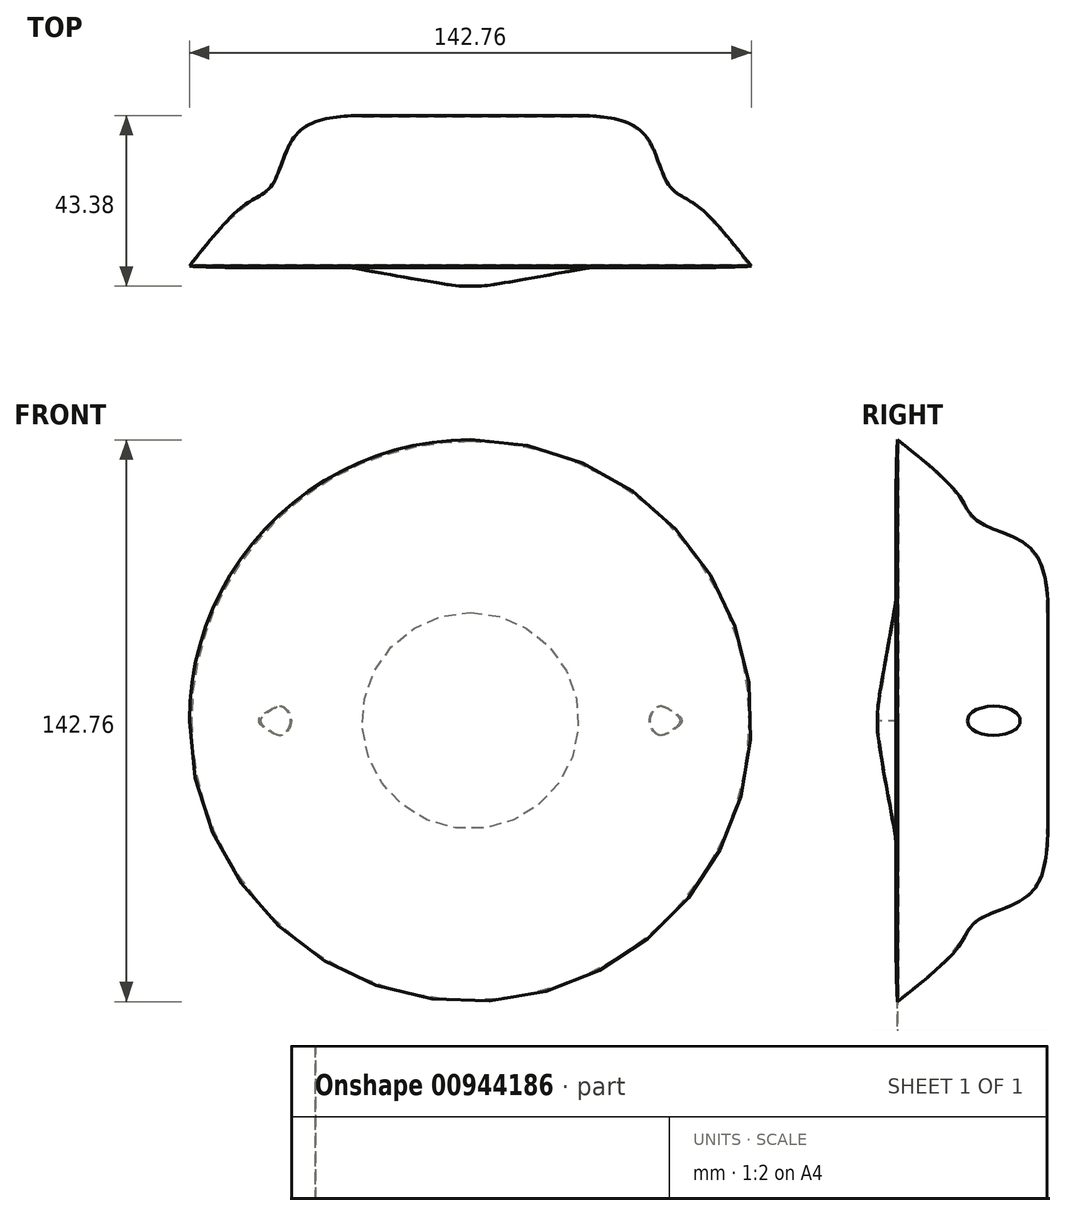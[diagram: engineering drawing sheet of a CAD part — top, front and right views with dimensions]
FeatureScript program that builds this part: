
annotation { "Feature Type Name" : "Feature", "Feature Type Description" : "" }
export const myFeature = defineFeature(function(context is Context, id is Id, definition is map)
    precondition{}
    {
        {
            var Q0;
            Q0=qCreatedBy(makeId("Top.planeOp"),FACE);
            var sketch = newSketch(context, id + "F0", { "sketchPlane" : qUnion([Q0])});
            skLineSegment(sketch, "E0", {"start": v(0, 53.6) * mm, "end": v(0, -40.76) * mm, "construction": true});
            skFitSpline(sketch, "E1", {"points": [v(-27.5, 27.9) * mm, v(-43.77, 23.5) * mm, v(-50.4, 10.24) * mm, v(-57.22, 5.22) * mm, v(-70.88, -9.86) * mm], "startDerivative": vector(-70.49, -0.68) * mm, "endDerivative": vector(-48.75, -61.1) * mm});
            skFitSpline(sketch, "E2", {"points": [v(-70.88, -9.86) * mm, v(-35.76, -9.86) * mm, v(-24.56, -11.24) * mm, v(-6.91, -14.34) * mm, v(0, -14.96) * mm], "startDerivative": vector(112.17, -6.42) * mm, "endDerivative": vector(40.87, 0.81) * mm});
            skFitSpline(sketch, "E3", {"points": [v(-27.5, 27.9) * mm, v(0, 27.9) * mm], "startDerivative": vector(26.1, 0) * mm, "endDerivative": vector(26.1, 0) * mm});
            skLineSegment(sketch, "E4", {"start": v(0, -14.96) * mm, "end": v(3.07, -14.96) * mm, "construction": true});
            skLineSegment(sketch, "E5", {"start": v(0, 27.9) * mm, "end": v(0, -14.96) * mm});
            skSolve(sketch);
        }
        {
            var Q0;
            Q0=makeQuery(id+"F0.imprint","IMPRINT",FACE,{"disambiguationData":[TD([[makeQuery(id+"F0.imprint","IMPRINT",EDGE,{"derivedFrom":sQuery(id+"F0.wireOp",EDGE,"E1")}),1.0]])]});
            var Q1;
            Q1=sQuery(id+"F0.wireOp",EDGE,"E0");
            revolve(context, id + "F1", {"surfaceOperationType" : NewSurfaceOperationType.NEW, "entities" : qUnion([Q0]), "axis" : qUnion([Q1]), "revolveType" : RevolveType.FULL});
        }
        {
            var Q0;
            Q0=qCreatedBy(makeId("Right.planeOp"),FACE);
            var sketch = newSketch(context, id + "F2", { "sketchPlane" : qUnion([Q0])});
            skLineSegment(sketch, "E6", {"start": v(28.83, 0) * mm, "end": v(0, 0) * mm, "construction": true});
            skEllipse(sketch, "E7", {"center": v(14.42, 0) * mm, "majorRadius": 6.75 * mm, "minorRadius": 3.72 * mm, "majorAxis": v(-1, 0)});
            skSolve(sketch);
        }
        {
            var Q0;
            Q0=makeQuery(id+"FU17nD5H0qyvq1o_1.2.F5.boolean.opBoolean","COPY",FACE,{"disambiguationData":[OD(1.0)],"derivedFrom":makeQuery(id+"FU17nD5H0qyvq1o_1.2.F5.opExtrude","SWEPT_FACE",FACE,{"disambiguationData":[OSD([sQuery(id+"F2.wireOp",EDGE,"E7")])]})});
            var Q1;
            Q1=makeQuery(id+"F1.opRevolve","SWEPT_BODY",BODY,{"disambiguationData":[OSD([sQuery(id+"F0.wireOp",EDGE,"E1"),sQuery(id+"F0.wireOp",EDGE,"E2"),sQuery(id+"F0.wireOp",EDGE,"E3"),sQuery(id+"F0.wireOp",EDGE,"E5")])]});
            shell(context, id + "F3", {"isHollow" : true, "entities" : qUnion([Q0]), "parts" : qUnion([Q1]), "thickness" : 0.25 * mm, "oppositeDirection" : true});
        }
        {
            var Q0;
            Q0=qCreatedBy(makeId("Top.planeOp"),FACE);
            var sketch = newSketch(context, id + "F4", { "sketchPlane" : qUnion([Q0])});
            skLineSegment(sketch, "E8", {"start": v(0, 74.25) * mm, "end": v(0, -46.57) * mm, "construction": true});
            skSolve(sketch);
        }
        {
            var Q0;
            Q0 = qSketchRegion(id + "F2", true);
            var Q1;
            Q1=sQuery(id+"F2.wireOp",EDGE,"E7");
            extrude(context, id + "F5", {"entities" : qUnion([Q0]), "operationType" : NewBodyOperationType.REMOVE, "surfaceEntities" : qUnion([Q1]), "endBound" : BoundingType.SYMMETRIC, "oppositeDirection" : true, "depth" : 131.57 * mm, "offsetDistance" : 25.4 * mm});
        }
    });
